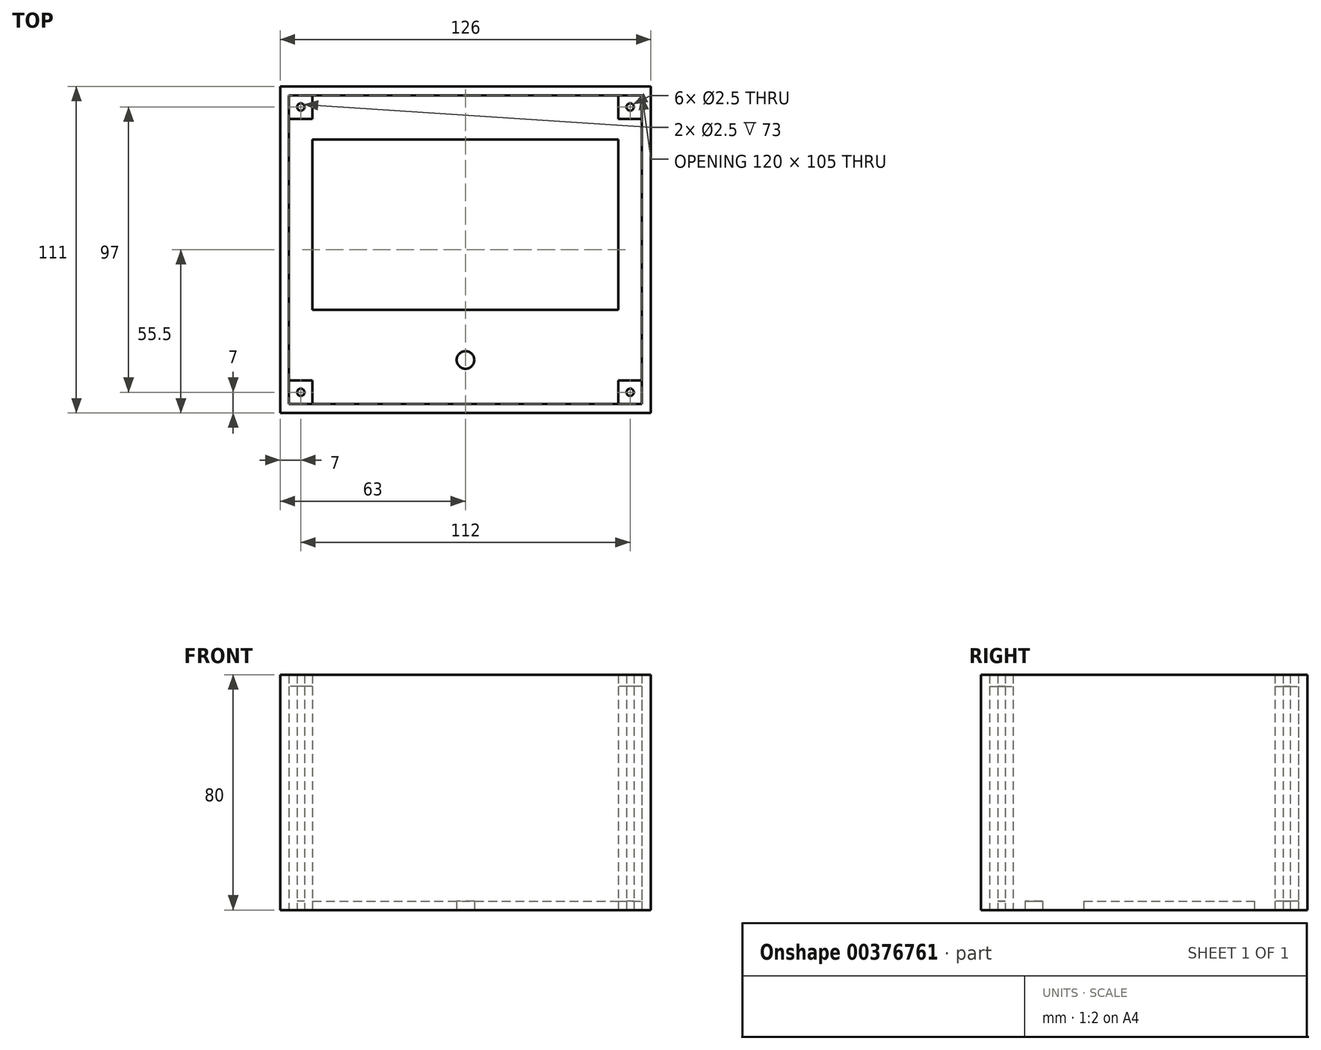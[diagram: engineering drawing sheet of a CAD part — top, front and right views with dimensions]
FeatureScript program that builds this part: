
annotation { "Feature Type Name" : "Feature", "Feature Type Description" : "" }
export const myFeature = defineFeature(function(context is Context, id is Id, definition is map)
    precondition{}
    {
        {
            var Q0;
            Q0=qCreatedBy(makeId("Top.planeOp"),FACE);
            var sketch = newSketch(context, id + "F0", { "sketchPlane" : qUnion([Q0])});
            skLineSegment(sketch, "E0.bottom", {"start": v(63, -55.5) * mm, "end": v(-63, -55.5) * mm});
            skLineSegment(sketch, "E0.top", {"start": v(63, 55.5) * mm, "end": v(-63, 55.5) * mm});
            skLineSegment(sketch, "E0.left", {"start": v(63, -55.5) * mm, "end": v(63, 55.5) * mm});
            skLineSegment(sketch, "E0.right", {"start": v(-63, -55.5) * mm, "end": v(-63, 55.5) * mm});
            skPoint(sketch, "E0.middle", {"position": v(0, 0) * mm});
            skLineSegment(sketch, "E1.0", {"start": v(60, -52.5) * mm, "end": v(-60, -52.5) * mm});
            skLineSegment(sketch, "E1.1", {"start": v(60, -52.5) * mm, "end": v(60, 52.5) * mm});
            skLineSegment(sketch, "E1.2", {"start": v(60, 52.5) * mm, "end": v(-60, 52.5) * mm});
            skLineSegment(sketch, "E1.3", {"start": v(-60, -52.5) * mm, "end": v(-60, 52.5) * mm});
            skLineSegment(sketch, "E2.bottom", {"start": v(60, 52.5) * mm, "end": v(52, 52.5) * mm});
            skLineSegment(sketch, "E2.top", {"start": v(60, 44.5) * mm, "end": v(52, 44.5) * mm});
            skLineSegment(sketch, "E2.left", {"start": v(60, 52.5) * mm, "end": v(60, 44.5) * mm});
            skLineSegment(sketch, "E2.right", {"start": v(52, 52.5) * mm, "end": v(52, 44.5) * mm});
            skLineSegment(sketch, "E3.MirrorCS", {"start": v(-52, 52.5) * mm, "end": v(-52, 44.5) * mm});
            skLineSegment(sketch, "E4.MirrorCS", {"start": v(-60, 52.5) * mm, "end": v(-52, 52.5) * mm});
            skLineSegment(sketch, "E5.MirrorCS", {"start": v(-60, 44.5) * mm, "end": v(-52, 44.5) * mm});
            skLineSegment(sketch, "E6.MirrorCS", {"start": v(-60, 52.5) * mm, "end": v(-60, 44.5) * mm});
            skLineSegment(sketch, "E7.MirrorCS", {"start": v(60, -44.5) * mm, "end": v(52, -44.5) * mm});
            skLineSegment(sketch, "E8.MirrorCS", {"start": v(60, -52.5) * mm, "end": v(60, -44.5) * mm});
            skLineSegment(sketch, "E9.MirrorCS", {"start": v(60, -52.5) * mm, "end": v(52, -52.5) * mm});
            skLineSegment(sketch, "E10.MirrorCS", {"start": v(52, -52.5) * mm, "end": v(52, -44.5) * mm});
            skLineSegment(sketch, "E11.MirrorCS", {"start": v(-60, -44.5) * mm, "end": v(-52, -44.5) * mm});
            skLineSegment(sketch, "E12.MirrorCS", {"start": v(-52, -52.5) * mm, "end": v(-52, -44.5) * mm});
            skCircle(sketch, "E13", {"center": v(-56, 48.5) * mm, "radius": 1.25 * mm});
            skCircle(sketch, "E14.MirrorC", {"center": v(56, 48.5) * mm, "radius": 1.25 * mm});
            skCircle(sketch, "E15.MirrorC", {"center": v(-56, -48.5) * mm, "radius": 1.25 * mm});
            skCircle(sketch, "E16.MirrorC", {"center": v(56, -48.5) * mm, "radius": 1.25 * mm});
            skLineSegment(sketch, "E17.bottom", {"start": v(-52, -20.5) * mm, "end": v(52, -20.5) * mm});
            skLineSegment(sketch, "E17.top", {"start": v(-52, 37.5) * mm, "end": v(52, 37.5) * mm});
            skLineSegment(sketch, "E17.left", {"start": v(-52, -20.5) * mm, "end": v(-52, 37.5) * mm});
            skLineSegment(sketch, "E17.right", {"start": v(52, -20.5) * mm, "end": v(52, 37.5) * mm});
            skCircle(sketch, "E18", {"center": v(0, -37.5) * mm, "radius": 3 * mm});
            skSolve(sketch);
        }
        {
            var Q0;
            Q0=makeQuery(id+"F0.imprint","IMPRINT",FACE,{"disambiguationData":[TD([[makeQuery(id+"F0.imprint","IMPRINT",EDGE,{"derivedFrom":sQuery(id+"F0.wireOp",EDGE,"E1.1")}),1.0]])]});
            var Q1;
            Q1=makeQuery(id+"F0.imprint","IMPRINT",FACE,{"disambiguationData":[TD([[makeQuery(id+"F0.imprint","IMPRINT",EDGE,{"derivedFrom":sQuery(id+"F0.wireOp",EDGE,"E0.bottom")}),-1.0]])]});
            var Q2;
            {var subQ0=sQuery(id+"F0.wireOp",EDGE,"E11.MirrorCS");Q2=makeQuery(id+"F0.imprint","IMPRINT",FACE,{"disambiguationData":[TD([[makeQuery(id+"F0.imprint","IMPRINT",EDGE,{"derivedFrom":subQ0}),-1.0]])]});}
            var Q3;
            Q3=makeQuery(id+"F0.imprint","IMPRINT",FACE,{"disambiguationData":[TD([[makeQuery(id+"F0.imprint","IMPRINT",EDGE,{"derivedFrom":sQuery(id+"F0.wireOp",EDGE,"E15.MirrorC")}),-1.0]])]});
            var Q4;
            Q4=makeQuery(id+"F0.imprint","IMPRINT",FACE,{"disambiguationData":[TD([[makeQuery(id+"F0.imprint","IMPRINT",EDGE,{"derivedFrom":sQuery(id+"F0.wireOp",EDGE,"E14.MirrorC")}),-1.0]])]});
            var Q5;
            Q5=makeQuery(id+"F0.imprint","IMPRINT",FACE,{"disambiguationData":[TD([[makeQuery(id+"F0.imprint","IMPRINT",EDGE,{"derivedFrom":sQuery(id+"F0.wireOp",EDGE,"E2.bottom")}),1.0]])]});
            var Q6;
            Q6=makeQuery(id+"F0.imprint","IMPRINT",FACE,{"disambiguationData":[TD([[makeQuery(id+"F0.imprint","IMPRINT",EDGE,{"derivedFrom":sQuery(id+"F0.wireOp",EDGE,"E13")}),1.0]])]});
            var Q7;
            Q7=makeQuery(id+"F0.imprint","IMPRINT",FACE,{"disambiguationData":[TD([[makeQuery(id+"F0.imprint","IMPRINT",EDGE,{"derivedFrom":sQuery(id+"F0.wireOp",EDGE,"E3.MirrorCS")}),-1.0]])]});
            var Q8;
            Q8=makeQuery(id+"F0.imprint","IMPRINT",FACE,{"disambiguationData":[TD([[makeQuery(id+"F0.imprint","IMPRINT",EDGE,{"derivedFrom":sQuery(id+"F0.wireOp",EDGE,"E16.MirrorC")}),1.0]])]});
            var Q9;
            Q9=makeQuery(id+"F0.imprint","IMPRINT",FACE,{"disambiguationData":[TD([[makeQuery(id+"F0.imprint","IMPRINT",EDGE,{"derivedFrom":sQuery(id+"F0.wireOp",EDGE,"E7.MirrorCS")}),1.0]])]});
            var Q10;
            Q10=makeQuery(id+"F0.imprint","IMPRINT",FACE,{"disambiguationData":[TD([[makeQuery(id+"F0.imprint","IMPRINT",EDGE,{"derivedFrom":sQuery(id+"F0.wireOp",EDGE,"E17.bottom")}),1.0]])]});
            var Q11;
            Q11=makeQuery(id+"F0.imprint","IMPRINT",FACE,{"disambiguationData":[TD([[makeQuery(id+"F0.imprint","IMPRINT",EDGE,{"derivedFrom":sQuery(id+"F0.wireOp",EDGE,"E18")}),1.0]])]});
            extrude(context, id + "F1", {"entities" : qUnion([Q0, Q1, Q2, Q3, Q4, Q5, Q6, Q7, Q8, Q9, Q10, Q11]), "depth" : 3 * mm});
        }
        {
            var Q0;
            Q0 = qSketchRegion(id + "F0", true);
            extrude(context, id + "F2", {"entities" : qUnion([Q0]), "operationType" : NewBodyOperationType.ADD, "depth" : 80 * mm});
        }
        {
            var Q0;
            Q0=makeQuery(id+"F0.imprint","IMPRINT",FACE,{"disambiguationData":[TD([[makeQuery(id+"F0.imprint","IMPRINT",EDGE,{"derivedFrom":sQuery(id+"F0.wireOp",EDGE,"E7.MirrorCS")}),1.0]])]});
            var Q1;
            Q1=makeQuery(id+"F0.imprint","IMPRINT",FACE,{"disambiguationData":[TD([[makeQuery(id+"F0.imprint","IMPRINT",EDGE,{"derivedFrom":sQuery(id+"F0.wireOp",EDGE,"E2.bottom")}),1.0]])]});
            var Q2;
            {var subQ0=sQuery(id+"F0.wireOp",EDGE,"E11.MirrorCS");Q2=makeQuery(id+"F0.imprint","IMPRINT",FACE,{"disambiguationData":[TD([[makeQuery(id+"F0.imprint","IMPRINT",EDGE,{"derivedFrom":subQ0}),-1.0]])]});}
            var Q3;
            Q3=makeQuery(id+"F0.imprint","IMPRINT",FACE,{"disambiguationData":[TD([[makeQuery(id+"F0.imprint","IMPRINT",EDGE,{"derivedFrom":sQuery(id+"F0.wireOp",EDGE,"E3.MirrorCS")}),-1.0]])]});
            extrude(context, id + "F3", {"entities" : qUnion([Q0, Q1, Q2, Q3]), "operationType" : NewBodyOperationType.ADD, "depth" : 76 * mm});
        }
        {
            var Q0;
            Q0=makeQuery(id+"F0.imprint","IMPRINT",FACE,{"disambiguationData":[TD([[makeQuery(id+"F0.imprint","IMPRINT",EDGE,{"derivedFrom":sQuery(id+"F0.wireOp",EDGE,"E1.1")}),1.0]])]});
            var Q1;
            {var subQ0=sQuery(id+"F0.wireOp",EDGE,"E11.MirrorCS");Q1=makeQuery(id+"F0.imprint","IMPRINT",FACE,{"disambiguationData":[TD([[makeQuery(id+"F0.imprint","IMPRINT",EDGE,{"derivedFrom":subQ0}),-1.0]])]});}
            var Q2;
            Q2=makeQuery(id+"F0.imprint","IMPRINT",FACE,{"disambiguationData":[TD([[makeQuery(id+"F0.imprint","IMPRINT",EDGE,{"derivedFrom":sQuery(id+"F0.wireOp",EDGE,"E3.MirrorCS")}),-1.0]])]});
            var Q3;
            Q3=makeQuery(id+"F0.imprint","IMPRINT",FACE,{"disambiguationData":[TD([[makeQuery(id+"F0.imprint","IMPRINT",EDGE,{"derivedFrom":sQuery(id+"F0.wireOp",EDGE,"E2.bottom")}),1.0]])]});
            var Q4;
            Q4=makeQuery(id+"F0.imprint","IMPRINT",FACE,{"disambiguationData":[TD([[makeQuery(id+"F0.imprint","IMPRINT",EDGE,{"derivedFrom":sQuery(id+"F0.wireOp",EDGE,"E7.MirrorCS")}),1.0]])]});
            extrude(context, id + "F4", {"entities" : qUnion([Q0, Q1, Q2, Q3, Q4]), "depth" : 4 * mm});
        }
        {
            var Q0;
            Q0=makeQuery(id+"F4.opExtrude","SWEPT_BODY",BODY,{"disambiguationData":[OSD([sQuery(id+"F0.wireOp",EDGE,"E1.0"),sQuery(id+"F0.wireOp",EDGE,"E1.1"),sQuery(id+"F0.wireOp",EDGE,"E1.2"),sQuery(id+"F0.wireOp",EDGE,"E1.3"),sQuery(id+"F0.wireOp",EDGE,"E2.bottom"),sQuery(id+"F0.wireOp",EDGE,"E2.left"),sQuery(id+"F0.wireOp",EDGE,"E4.MirrorCS"),sQuery(id+"F0.wireOp",EDGE,"E6.MirrorCS"),sQuery(id+"F0.wireOp",EDGE,"E8.MirrorCS"),sQuery(id+"F0.wireOp",EDGE,"E9.MirrorCS")])]});
            var Q1;
            Q1=makeQuery(id+"F3.boolean.opBoolean","SPLIT",FACE,{"disambiguationData":[TD([makeQuery(id+"F3.opExtrude","SWEPT_FACE",FACE,{"disambiguationData":[OSD([sQuery(id+"F0.wireOp",EDGE,"E2.top")])]})])],"derivedFrom":makeQuery(id+"F1.opExtrude","CAP_FACE",FACE,{"disambiguationData":[OSD([sQuery(id+"F0.wireOp",EDGE,"E0.bottom"),sQuery(id+"F0.wireOp",EDGE,"E0.top"),sQuery(id+"F0.wireOp",EDGE,"E0.left"),sQuery(id+"F0.wireOp",EDGE,"E0.right")])],"isStart":false})});
            transform(context, id + "F5", {"entities" : qUnion([Q0]), "transformType" : TransformType.TRANSLATION_DISTANCE, "transformDirection" : qUnion([Q1]), "distance" : 76 * mm, "makeCopy" : false});
        }
    });
